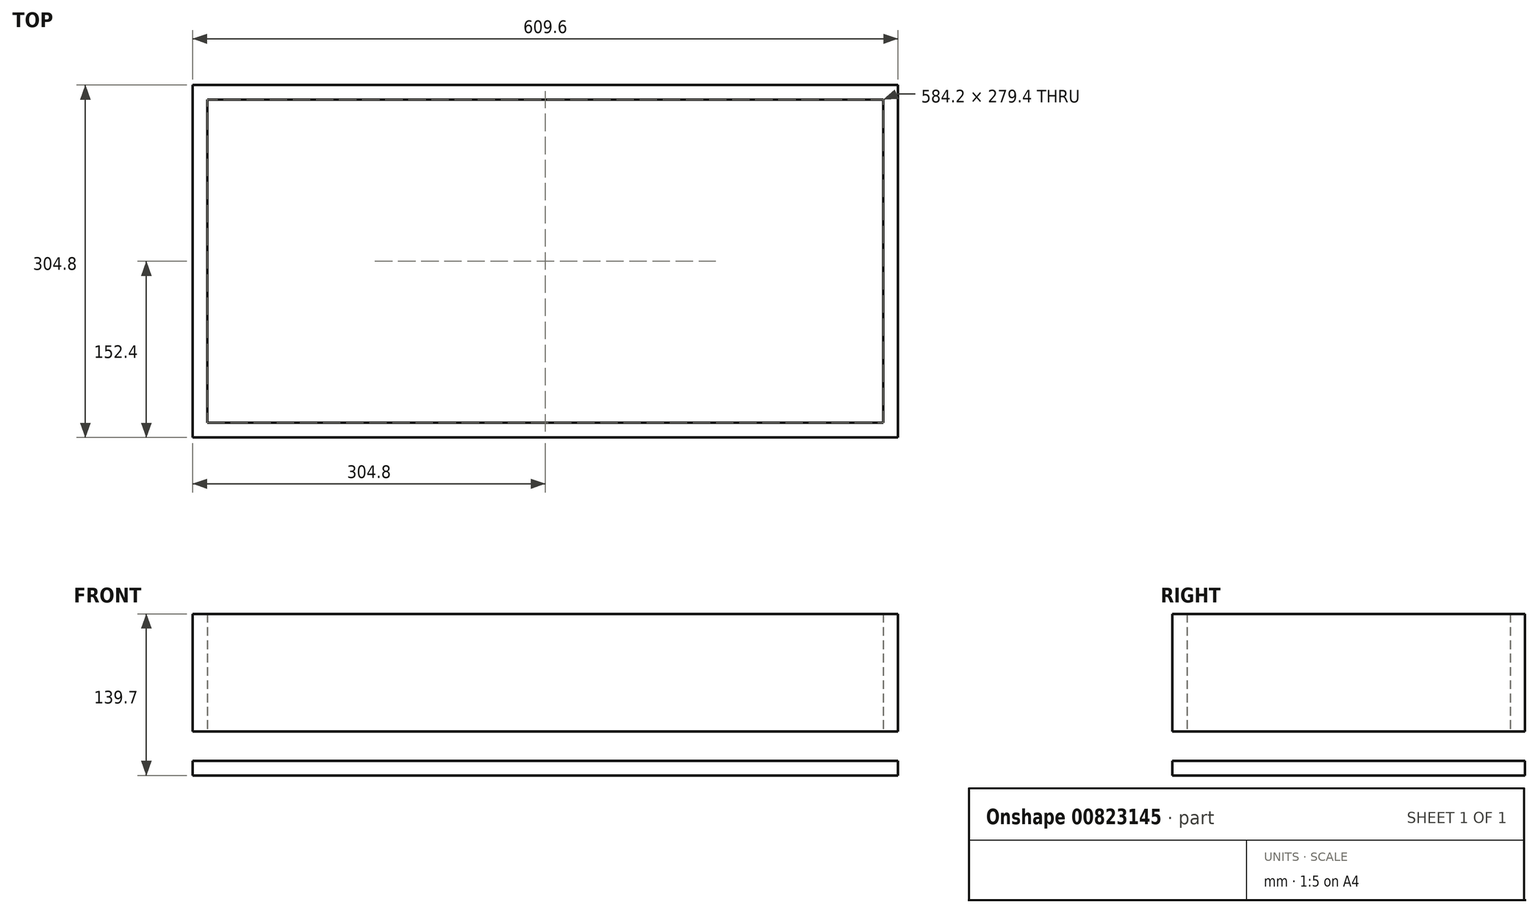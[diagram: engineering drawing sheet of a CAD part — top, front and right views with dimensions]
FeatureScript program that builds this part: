
annotation { "Feature Type Name" : "Feature", "Feature Type Description" : "" }
export const myFeature = defineFeature(function(context is Context, id is Id, definition is map)
    precondition{}
    {
        {
            var Q0;
            Q0=qCreatedBy(makeId("Top.planeOp"),FACE);
            var sketch = newSketch(context, id + "F0", { "sketchPlane" : qUnion([Q0])});
            skLineSegment(sketch, "E0.bottom", {"start": v(0, 0) * mm, "end": v(609.6, 0) * mm});
            skLineSegment(sketch, "E0.top", {"start": v(0, 304.8) * mm, "end": v(609.6, 304.8) * mm});
            skLineSegment(sketch, "E0.left", {"start": v(0, 0) * mm, "end": v(0, 304.8) * mm});
            skLineSegment(sketch, "E0.right", {"start": v(609.6, 0) * mm, "end": v(609.6, 304.8) * mm});
            skSolve(sketch);
        }
        {
            var Q0;
            Q0=makeQuery(id+"F0.imprint","IMPRINT",FACE,{"disambiguationData":[TD([[makeQuery(id+"F0.imprint","IMPRINT",EDGE,{"derivedFrom":sQuery(id+"F0.wireOp",EDGE,"E0.bottom")}),1.0]])]});
            extrude(context, id + "F1", {"entities" : qUnion([Q0]), "depth" : 12.7 * mm, "offsetDistance" : 25.4 * mm});
        }
        {
            var Q0;
            Q0=makeQuery(id+"F1.opExtrude","CAP_FACE",FACE,{"disambiguationData":[OSD([sQuery(id+"F0.wireOp",EDGE,"E0.bottom"),sQuery(id+"F0.wireOp",EDGE,"E0.top"),sQuery(id+"F0.wireOp",EDGE,"E0.left"),sQuery(id+"F0.wireOp",EDGE,"E0.right")])],"isStart":false});
            cPlane(context, id + "F2", {"entities" : qUnion([Q0]), "cplaneType" : CPlaneType.OFFSET, "offset" : 25.4 * mm, "width" : 152.4 * mm, "height" : 152.4 * mm});
        }
        {
            var Q0;
            Q0=qCreatedBy(id+"F2.planeOp",FACE);
            var sketch = newSketch(context, id + "F3", { "sketchPlane" : qUnion([Q0])});
            skLineSegment(sketch, "E1.bottom", {"start": v(0, 0) * mm, "end": v(12.7, 0) * mm});
            skLineSegment(sketch, "E1.top", {"start": v(0, 304.8) * mm, "end": v(12.7, 304.8) * mm});
            skLineSegment(sketch, "E1.left", {"start": v(0, 0) * mm, "end": v(0, 304.8) * mm});
            skLineSegment(sketch, "E1.right", {"start": v(12.7, 0) * mm, "end": v(12.7, 304.8) * mm});
            skLineSegment(sketch, "E2.bottom", {"start": v(12.7, 0) * mm, "end": v(596.9, 0) * mm});
            skLineSegment(sketch, "E2.top", {"start": v(12.7, 12.7) * mm, "end": v(596.9, 12.7) * mm});
            skLineSegment(sketch, "E2.left", {"start": v(12.7, 0) * mm, "end": v(12.7, 12.7) * mm});
            skLineSegment(sketch, "E2.right", {"start": v(596.9, 0) * mm, "end": v(596.9, 12.7) * mm});
            skLineSegment(sketch, "E3.bottom", {"start": v(596.9, 0) * mm, "end": v(609.6, 0) * mm});
            skLineSegment(sketch, "E3.top", {"start": v(596.9, 304.8) * mm, "end": v(609.6, 304.8) * mm});
            skLineSegment(sketch, "E3.left", {"start": v(596.9, 0) * mm, "end": v(596.9, 304.8) * mm});
            skLineSegment(sketch, "E3.right", {"start": v(609.6, 0) * mm, "end": v(609.6, 304.8) * mm});
            skLineSegment(sketch, "E4.bottom", {"start": v(12.7, 304.8) * mm, "end": v(596.9, 304.8) * mm});
            skLineSegment(sketch, "E4.top", {"start": v(12.7, 292.1) * mm, "end": v(596.9, 292.1) * mm});
            skLineSegment(sketch, "E4.left", {"start": v(12.7, 304.8) * mm, "end": v(12.7, 292.1) * mm});
            skLineSegment(sketch, "E4.right", {"start": v(596.9, 304.8) * mm, "end": v(596.9, 292.1) * mm});
            skSolve(sketch);
        }
        {
            var Q0;
            {var subQ0=sQuery(id+"F3.wireOp",EDGE,"E2.bottom");Q0=makeQuery(id+"F3.imprint","IMPRINT",FACE,{"disambiguationData":[TD([[makeQuery(id+"F3.imprint","IMPRINT",EDGE,{"derivedFrom":subQ0}),1.0]])]});}
            var Q1;
            Q1=makeQuery(id+"F3.imprint","IMPRINT",FACE,{"disambiguationData":[TD([[makeQuery(id+"F3.imprint","IMPRINT",EDGE,{"derivedFrom":sQuery(id+"F3.wireOp",EDGE,"E4.bottom")}),-1.0]])]});
            var Q2;
            Q2=makeQuery(id+"F3.imprint","IMPRINT",FACE,{"disambiguationData":[TD([[makeQuery(id+"F3.imprint","IMPRINT",EDGE,{"derivedFrom":sQuery(id+"F3.wireOp",EDGE,"E1.bottom")}),1.0]])]});
            var Q3;
            {var subQ3=sQuery(id+"F3.wireOp",EDGE,"E3.bottom");Q3=makeQuery(id+"F3.imprint","IMPRINT",FACE,{"disambiguationData":[TD([[makeQuery(id+"F3.imprint","IMPRINT",EDGE,{"derivedFrom":subQ3}),1.0]])]});}
            extrude(context, id + "F4", {"entities" : qUnion([Q0, Q1, Q2, Q3]), "depth" : 101.6 * mm, "offsetDistance" : 25.4 * mm});
        }
    });
